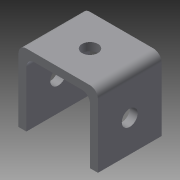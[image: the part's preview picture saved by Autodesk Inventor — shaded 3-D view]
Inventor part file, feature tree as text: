
AUTODESK INVENTOR PART (.ipt)
format: ipt  version: 2015 (Build 190159000, 159)  size: 402,944 bytes
history: native  units: in
note: dims shown in document units (in); Inventor stores cm internally (conversion verified against a paired STEP export)
features: extrude x3, sketch x3, pattern_linear x1
ambient origin geometry x8: Origin, YZ Plane, XZ Plane, XY Plane, X Axis, Y Axis, Z Axis, Center Point
bodies: Solid1 (feature_tree)
feature tree (7):
  extrude  "Extrusion1"  Depth=1.0in
  extrude  "Extrusion4"  Depth=0.5in
  pattern_linear  "Rectangular Pattern3"  Spacing1=0.25in  [1 undecoded]
  extrude  "Extrusion5"  Depth=1.0in TaperAngle=0.0deg
  sketch  "Sketch1"  dims[d0=1.13in d1=1.25in d2=0.125in d3=0.125in d4=0.125in d5=1.0in]
  sketch  "Sketch4"  dims[d6=0.0in d34=0.5in]
  sketch  "Sketch5"  dims[d35=0.0in d36=0.25in d37=1.0in d38=0.0in d39=11.811in d41=1.0in d42=11.811in d44=1.0in d45=0.25in d46=1.0in d47=0.0in]
note: 1 required parameter value undecoded (feature->parameter linkage not recoverable at this tier; creation-order binding heuristic only, values carry confidence <= 0.55)
